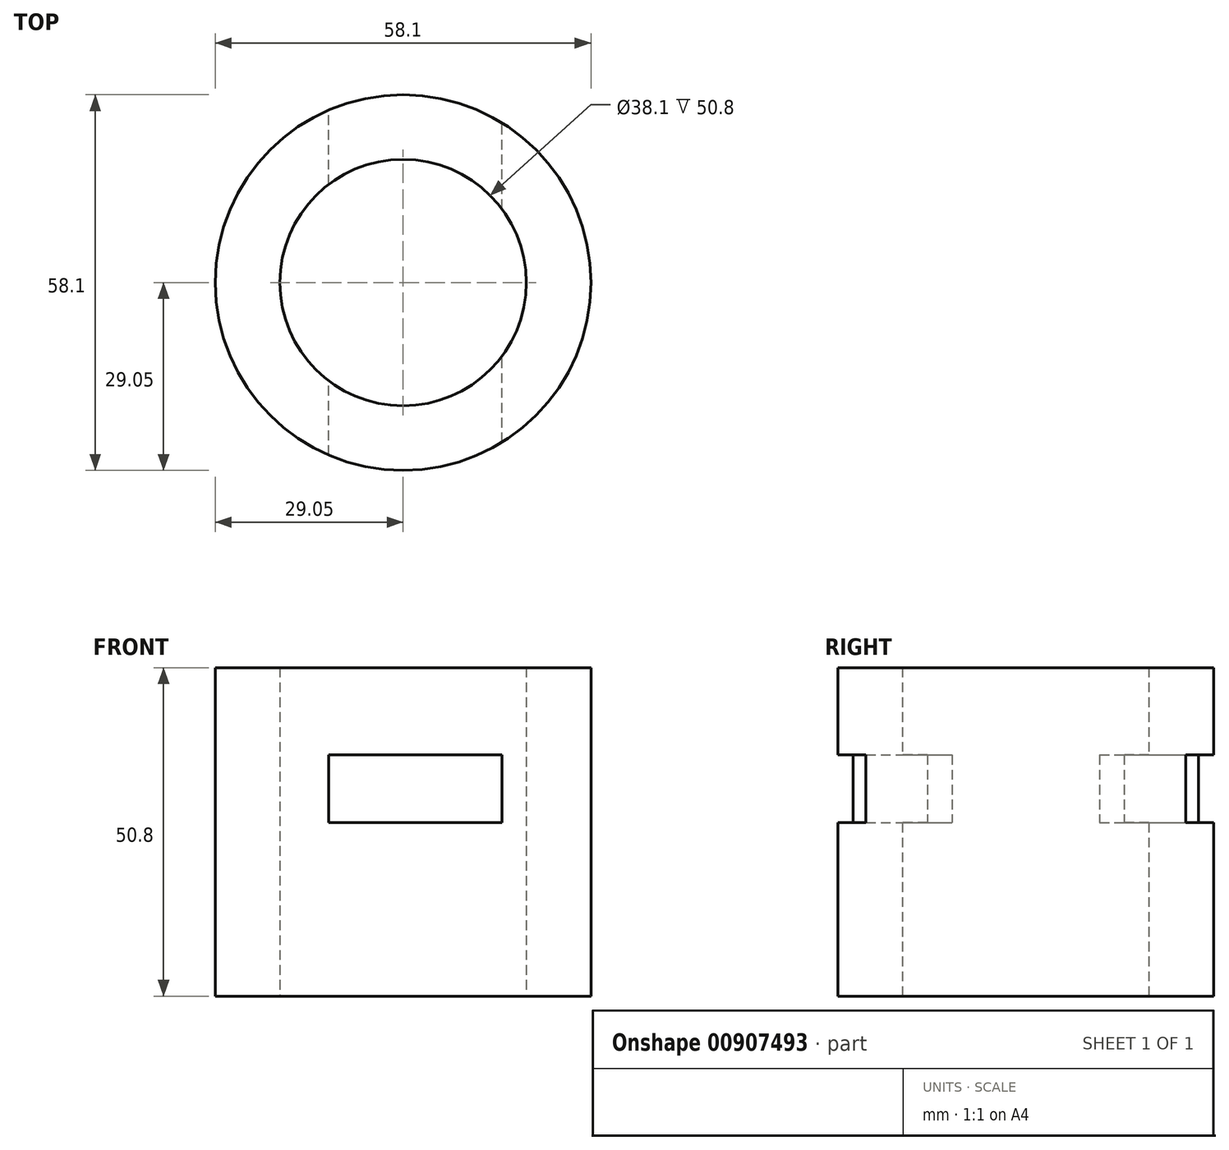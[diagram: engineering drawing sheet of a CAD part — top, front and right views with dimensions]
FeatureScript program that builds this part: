
annotation { "Feature Type Name" : "Feature", "Feature Type Description" : "" }
export const myFeature = defineFeature(function(context is Context, id is Id, definition is map)
    precondition{}
    {
        {
            var Q0;
            Q0=qCreatedBy(makeId("Top.planeOp"),FACE);
            var sketch = newSketch(context, id + "F0", { "sketchPlane" : qUnion([Q0])});
            skCircle(sketch, "E0", {"center": v(0, 0) * mm, "radius": 19.05 * mm});
            skCircle(sketch, "E1.0", {"center": v(0, 0) * mm, "radius": 29.05 * mm});
            skSolve(sketch);
        }
        {
            var Q0;
            Q0=makeQuery(id+"F0.imprint","IMPRINT",FACE,{"disambiguationData":[TD([[makeQuery(id+"F0.imprint","IMPRINT",EDGE,{"derivedFrom":sQuery(id+"F0.wireOp",EDGE,"E0")}),-1.0]])]});
            extrude(context, id + "F1", {"entities" : qUnion([Q0]), "depth" : 50.8 * mm, "offsetDistance" : 25.4 * mm});
        }
        {
            var Q0;
            Q0=qCreatedBy(makeId("Front.planeOp"),FACE);
            var sketch = newSketch(context, id + "F2", { "sketchPlane" : qUnion([Q0])});
            skLineSegment(sketch, "E2.bottom", {"start": v(-11.5, 26.8) * mm, "end": v(15.27, 26.8) * mm});
            skLineSegment(sketch, "E2.top", {"start": v(-11.5, 37.28) * mm, "end": v(15.27, 37.28) * mm});
            skLineSegment(sketch, "E2.left", {"start": v(-11.5, 26.8) * mm, "end": v(-11.5, 37.28) * mm});
            skLineSegment(sketch, "E2.right", {"start": v(15.27, 26.8) * mm, "end": v(15.27, 37.28) * mm});
            skSolve(sketch);
        }
        {
            var Q0;
            Q0=makeQuery(id+"F2.imprint","IMPRINT",FACE,{"disambiguationData":[TD([[makeQuery(id+"F2.imprint","IMPRINT",EDGE,{"derivedFrom":sQuery(id+"F2.wireOp",EDGE,"E2.bottom")}),1.0]])]});
            extrude(context, id + "F3", {"entities" : qUnion([Q0]), "endBound" : BoundingType.SYMMETRIC, "depth" : 101.6 * mm, "offsetDistance" : 25.4 * mm});
        }
        {
            var Q0;
            Q0=makeQuery(id+"F3.opExtrude","SWEPT_BODY",BODY,{"disambiguationData":[OSD([sQuery(id+"F2.wireOp",EDGE,"E2.bottom"),sQuery(id+"F2.wireOp",EDGE,"E2.top"),sQuery(id+"F2.wireOp",EDGE,"E2.left"),sQuery(id+"F2.wireOp",EDGE,"E2.right")])]});
            var Q1;
            Q1=makeQuery(id+"F1.opExtrude","SWEPT_BODY",BODY,{"disambiguationData":[OSD([sQuery(id+"F0.wireOp",EDGE,"E0"),sQuery(id+"F0.wireOp",EDGE,"E1.0")])]});
            booleanBodies(context, id + "F4", {"operationType" : BooleanOperationType.SUBTRACTION, "tools" : qUnion([Q0]), "targets" : qUnion([Q1])});
        }
    });
